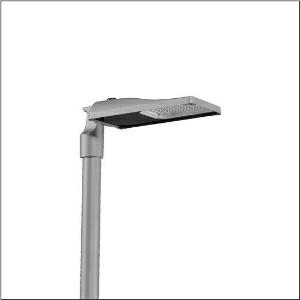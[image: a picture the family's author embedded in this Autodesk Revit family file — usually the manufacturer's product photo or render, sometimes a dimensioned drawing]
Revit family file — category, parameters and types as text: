
# Revit family: streetlight_sl_31_mini___st1_0a_5xh2d3as08ja_29fe
name_source: partatom
category: Lighting Fixtures
units: mm (PartAtom-declared; Revit-internal decimal feet)

## family parameters
Cut with Voids When Loaded = No
Host = Face
Light Source = No
Part Type = Normal
Room Calculation Point = No
Round Connector Dimension = Use Diameter
Shared = No

## types (1)
- --- (1 x LED, 12270 lm, 82.5 W, 3000K)
    Apparent Load = 83 VA
    CIE Flux Codes = 40 73 97 100 100
    Color Rendering = 70
    Color Temperature = 3000K
    Default Elevation = 1800 mm
    Description = Streetlight SL 31 mini D4i mast luminaire for post-top, side-entry; light control with lens of PMMA; light distribution: ST1.0a, direct asymmetric distribution, for standard-compliant lighting for roads and squares; LED: luminous flux: 12.270lm, light colour: 730, colour temperature: 3000K; luminous efficacy: 148,7lm/W; control: pre-setting: logarithmic dimming characteristic, flexible luminous flux parameterisation, time-dependent luminous flux control, constant luminous flux control, power reduction, intelligent temperature release in ECG and LED module, overheat protection; luminaire housing, of diecast aluminium, SITECO metallic grey (DB 702S), corrosivity category C5 high according to DIN EN ISO 12944; cover of toughened safety glass, transparent, mast flange of diecast aluminium, SITECO metallic grey (DB 702S), spigot size: 76/60mm, mast flange included unmounted; cable length: 10,5m, connection cable pre-assembled; mains connection: 220..240V, AC, 50/60Hz; power consumption (at start of service life): 82,5W / (at end of service life): 90,1W / (with reduced operation 50%): 36,8W; protection rating (complete): IP66; insulation class (complete): insulation class II (safety insulation); impact resistance: IK10; certification: CE, ENEC, ENEC+, VDE, UKCA, ZD4i; permissible operating ambient temperature for outdoor applications: -40..+50°C; packaging unit: 1 piece

Light Distribution: ST1.0a
    Height = 76 mm
    Lamp = 1 x LED
    Lamp Light Flux = 12270 lm
    Lamp Power = 82.5 W
    Lamp count = 1
    Length = 547 mm
    Luminous efficacy = 149 lm/W
    Manufacturer = Siteco
    ModVariant = No
    Model = 5XH2D3AS08JA
    Number of Poles = 1
    OnlyDefault = Yes
    Power Factor = 1
    Product Name = Streetlight SL 31 mini | ST1.0a
    Product group = mast luminaire | pylon top
    ProductGroupID = 6100
    Protection Class = Protection class II
    Protection Degree = IP 66
    RLX_Detail_Level = 1
    RLX_Emergency_Light_Flux = 0 lm
    RLX_Emergency_Type = 0
    RLX_Emergency_Type_DB = No
    RlxData = <blob elided: 39637 chars, md5=695cb9a1>
    Socket = socket
    Standby Power = 0 W
    System Light Flux = 12270 lm
    System Power = 83 W
    Type Comments = factory setting: luminous flux: 100 % | dim-lin: 254 | 870 mA
    Type Image = l_1300330.jpg
    URL = http://relux.com
    VarID = @adj_057675
    Voltage = 0 V
    Weight = 0.00 kg
    Width = 265 mm

## geometry (parser evidence)
native form markers: Blend x4, Sweep x11
no freeform markers — native parametric forms only
